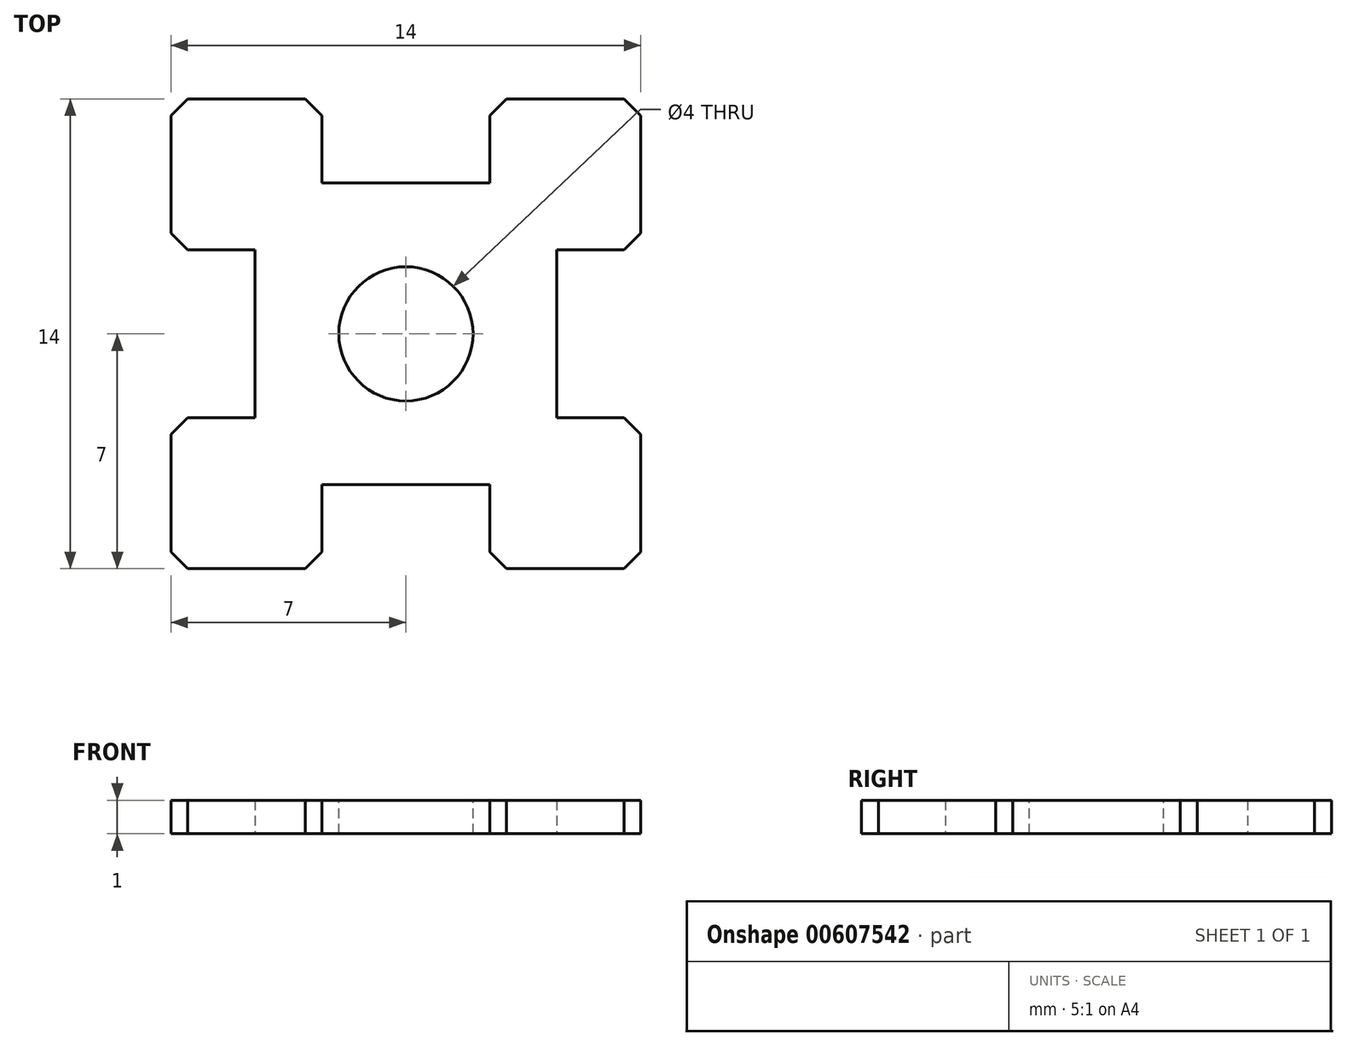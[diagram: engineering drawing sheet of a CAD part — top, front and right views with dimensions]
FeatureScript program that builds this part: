
annotation { "Feature Type Name" : "Feature", "Feature Type Description" : "" }
export const myFeature = defineFeature(function(context is Context, id is Id, definition is map)
    precondition{}
    {
        {
            var Q0;
            Q0=qCreatedBy(makeId("Top.planeOp"),FACE);
            var sketch = newSketch(context, id + "F0", { "sketchPlane" : qUnion([Q0])});
            skLineSegment(sketch, "E0.bottom", {"start": v(-7, -7) * mm, "end": v(-2.5, -7) * mm});
            skLineSegment(sketch, "E0.top", {"start": v(-7, 7) * mm, "end": v(-2.5, 7) * mm});
            skLineSegment(sketch, "E0.left", {"start": v(-7, -7) * mm, "end": v(-7, -2.5) * mm});
            skLineSegment(sketch, "E0.right", {"start": v(7, -7) * mm, "end": v(7, -2.5) * mm});
            skPoint(sketch, "E0.middle", {"position": v(0, 0) * mm});
            skLineSegment(sketch, "E1", {"start": v(0, 7) * mm, "end": v(0, -7) * mm, "construction": true});
            skLineSegment(sketch, "E2", {"start": v(-7, 0) * mm, "end": v(7, 0) * mm, "construction": true});
            skPoint(sketch, "E3.middle", {"position": v(0, -7) * mm});
            skLineSegment(sketch, "E4.top", {"start": v(-4.5, 2.5) * mm, "end": v(-7, 2.5) * mm});
            skLineSegment(sketch, "E4.left", {"start": v(-4.5, -2.5) * mm, "end": v(-4.5, 2.5) * mm});
            skPoint(sketch, "E4.middle", {"position": v(-7, 0) * mm});
            skLineSegment(sketch, "E5.bottom", {"start": v(-2.5, 4.5) * mm, "end": v(2.5, 4.5) * mm});
            skLineSegment(sketch, "E5.left", {"start": v(-2.5, 4.5) * mm, "end": v(-2.5, 7) * mm});
            skLineSegment(sketch, "E5.right", {"start": v(2.5, 4.5) * mm, "end": v(2.5, 7) * mm});
            skPoint(sketch, "E5.middle", {"position": v(0, 7) * mm});
            skPoint(sketch, "E6.middle", {"position": v(7, 0) * mm});
            skPoint(sketch, "E6.right.end.orphan", {"position": v(9.68, 2.5) * mm});
            skPoint(sketch, "E7.orphan", {"position": v(9.68, -2.5) * mm});
            skPoint(sketch, "E8.orphan", {"position": v(4.32, 2.5) * mm});
            skPoint(sketch, "E6.left.start.orphan", {"position": v(4.32, -2.5) * mm});
            skPoint(sketch, "E9.orphan", {"position": v(2.5, -4.92) * mm});
            skPoint(sketch, "E3.top.end.orphan", {"position": v(2.5, -9.08) * mm});
            skPoint(sketch, "E10.orphan", {"position": v(-2.5, -9.08) * mm});
            skPoint(sketch, "E3.left.start.orphan", {"position": v(-2.5, -4.92) * mm});
            skLineSegment(sketch, "E11.MirrorCS", {"start": v(4.5, -2.5) * mm, "end": v(4.5, 2.5) * mm});
            skLineSegment(sketch, "E12.MirrorCS", {"start": v(4.5, 2.5) * mm, "end": v(7, 2.5) * mm});
            skLineSegment(sketch, "E13.MirrorCS", {"start": v(4.5, -2.5) * mm, "end": v(4.5, 2.5) * mm, "construction": true});
            skLineSegment(sketch, "E14.MirrorCS", {"start": v(4.5, -2.5) * mm, "end": v(7, -2.5) * mm});
            skLineSegment(sketch, "E15.MirrorCS", {"start": v(-2.5, -4.5) * mm, "end": v(2.5, -4.5) * mm});
            skLineSegment(sketch, "E16.MirrorCS", {"start": v(-2.5, -4.5) * mm, "end": v(-2.5, -7) * mm});
            skLineSegment(sketch, "E17.MirrorCS", {"start": v(2.5, -4.5) * mm, "end": v(2.5, -7) * mm});
            skPoint(sketch, "E5.top.start.orphan", {"position": v(-2.5, 9.5) * mm});
            skPoint(sketch, "E18.orphan", {"position": v(2.5, 9.5) * mm});
            skPoint(sketch, "E19.orphan", {"position": v(9.5, 2.5) * mm});
            skPoint(sketch, "E20.orphan", {"position": v(9.5, -2.5) * mm});
            skLineSegment(sketch, "E21.trimOffspring", {"start": v(2.5, -9.08) * mm, "end": v(2.5, -9.5) * mm, "construction": true});
            skPoint(sketch, "E22.MirrorCS.end.orphan", {"position": v(2.5, -9.5) * mm});
            skPoint(sketch, "E22.MirrorCS.start.orphan", {"position": v(-2.5, -9.5) * mm});
            skLineSegment(sketch, "E23.trimOffspring", {"start": v(-2.5, -9.08) * mm, "end": v(-2.5, -9.5) * mm, "construction": true});
            skPoint(sketch, "E4.bottom.end.orphan", {"position": v(-9.5, -2.5) * mm});
            skPoint(sketch, "E24.orphan", {"position": v(-9.5, 2.5) * mm});
            skLineSegment(sketch, "E25", {"start": v(-4.5, -2.5) * mm, "end": v(-7, -2.5) * mm});
            skLineSegment(sketch, "E26.trimOffspring", {"start": v(2.5, 7) * mm, "end": v(7, 7) * mm});
            skLineSegment(sketch, "E27.trimOffspring", {"start": v(-7, 2.5) * mm, "end": v(-7, 7) * mm});
            skLineSegment(sketch, "E28.trimOffspring", {"start": v(2.5, -7) * mm, "end": v(7, -7) * mm});
            skLineSegment(sketch, "E29.trimOffspring", {"start": v(7, 2.5) * mm, "end": v(7, 7) * mm});
            skSolve(sketch);
        }
        {
            var Q0;
            Q0=makeQuery(id+"F0.imprint","IMPRINT",FACE,{"disambiguationData":[TD([[makeQuery(id+"F0.imprint","IMPRINT",EDGE,{"derivedFrom":sQuery(id+"F0.wireOp",EDGE,"E0.top")}),-1.0]])]});
            extrude(context, id + "F1", {"entities" : qUnion([Q0]), "depth" : 1 * mm, "offsetDistance" : 25 * mm});
        }
        {
            var Q0;
            Q0=makeQuery(id+"F1.opExtrude","SWEPT_EDGE",EDGE,{"disambiguationData":[OSD([sQuery(id+"F0.wireOp",EDGE,"E0.left"),sQuery(id+"F0.wireOp",EDGE,"E0.bottom")])]});
            var Q1;
            Q1=makeQuery(id+"F1.opExtrude","SWEPT_EDGE",EDGE,{"disambiguationData":[OSD([sQuery(id+"F0.wireOp",EDGE,"E0.bottom"),sQuery(id+"F0.wireOp",EDGE,"E16.MirrorCS")])]});
            var Q2;
            Q2=makeQuery(id+"F1.opExtrude","SWEPT_EDGE",EDGE,{"disambiguationData":[OSD([sQuery(id+"F0.wireOp",EDGE,"E0.left"),sQuery(id+"F0.wireOp",EDGE,"E25")])]});
            var Q3;
            Q3=makeQuery(id+"F1.opExtrude","SWEPT_EDGE",EDGE,{"disambiguationData":[OSD([sQuery(id+"F0.wireOp",EDGE,"E4.top"),sQuery(id+"F0.wireOp",EDGE,"E27.trimOffspring")])]});
            var Q4;
            Q4=makeQuery(id+"F1.opExtrude","SWEPT_EDGE",EDGE,{"disambiguationData":[OSD([sQuery(id+"F0.wireOp",EDGE,"E0.top"),sQuery(id+"F0.wireOp",EDGE,"E27.trimOffspring")])]});
            var Q5;
            Q5=makeQuery(id+"F1.opExtrude","SWEPT_EDGE",EDGE,{"disambiguationData":[OSD([sQuery(id+"F0.wireOp",EDGE,"E0.top"),sQuery(id+"F0.wireOp",EDGE,"E5.left")])]});
            var Q6;
            Q6=makeQuery(id+"F1.opExtrude","SWEPT_EDGE",EDGE,{"disambiguationData":[OSD([sQuery(id+"F0.wireOp",EDGE,"E5.right"),sQuery(id+"F0.wireOp",EDGE,"E26.trimOffspring")])]});
            var Q7;
            Q7=makeQuery(id+"F1.opExtrude","SWEPT_EDGE",EDGE,{"disambiguationData":[OSD([sQuery(id+"F0.wireOp",EDGE,"E26.trimOffspring"),sQuery(id+"F0.wireOp",EDGE,"E29.trimOffspring")])]});
            var Q8;
            Q8=makeQuery(id+"F1.opExtrude","SWEPT_EDGE",EDGE,{"disambiguationData":[OSD([sQuery(id+"F0.wireOp",EDGE,"E0.right"),sQuery(id+"F0.wireOp",EDGE,"E14.MirrorCS")])]});
            var Q9;
            Q9=makeQuery(id+"F1.opExtrude","SWEPT_EDGE",EDGE,{"disambiguationData":[OSD([sQuery(id+"F0.wireOp",EDGE,"E0.right"),sQuery(id+"F0.wireOp",EDGE,"E28.trimOffspring")])]});
            var Q10;
            Q10=makeQuery(id+"F1.opExtrude","SWEPT_EDGE",EDGE,{"disambiguationData":[OSD([sQuery(id+"F0.wireOp",EDGE,"E17.MirrorCS"),sQuery(id+"F0.wireOp",EDGE,"E28.trimOffspring")])]});
            var Q11;
            Q11=makeQuery(id+"F1.opExtrude","SWEPT_EDGE",EDGE,{"disambiguationData":[OSD([sQuery(id+"F0.wireOp",EDGE,"E12.MirrorCS"),sQuery(id+"F0.wireOp",EDGE,"E29.trimOffspring")])]});
            chamfer(context, id + "F2", {"entities" : qUnion([Q0, Q1, Q2, Q3, Q4, Q5, Q6, Q7, Q8, Q9, Q10, Q11]), "width" : 0.5 * mm, "tangentPropagation" : true});
        }
        {
            var Q0;
            Q0=makeQuery(id+"F1.opExtrude","CAP_FACE",FACE,{"disambiguationData":[OSD([sQuery(id+"F0.wireOp",EDGE,"E0.top"),sQuery(id+"F0.wireOp",EDGE,"E0.left"),sQuery(id+"F0.wireOp",EDGE,"E0.right"),sQuery(id+"F0.wireOp",EDGE,"E4.top"),sQuery(id+"F0.wireOp",EDGE,"E4.left"),sQuery(id+"F0.wireOp",EDGE,"E5.bottom"),sQuery(id+"F0.wireOp",EDGE,"E5.left"),sQuery(id+"F0.wireOp",EDGE,"E5.right"),sQuery(id+"F0.wireOp",EDGE,"E11.MirrorCS"),sQuery(id+"F0.wireOp",EDGE,"E12.MirrorCS"),sQuery(id+"F0.wireOp",EDGE,"E14.MirrorCS"),sQuery(id+"F0.wireOp",EDGE,"E15.MirrorCS"),sQuery(id+"F0.wireOp",EDGE,"E0.bottom"),sQuery(id+"F0.wireOp",EDGE,"E16.MirrorCS"),sQuery(id+"F0.wireOp",EDGE,"E17.MirrorCS"),sQuery(id+"F0.wireOp",EDGE,"E25"),sQuery(id+"F0.wireOp",EDGE,"E26.trimOffspring"),sQuery(id+"F0.wireOp",EDGE,"E27.trimOffspring"),sQuery(id+"F0.wireOp",EDGE,"E28.trimOffspring"),sQuery(id+"F0.wireOp",EDGE,"E29.trimOffspring")])],"isStart":false});
            var sketch = newSketch(context, id + "F3", { "sketchPlane" : qUnion([Q0])});
            skCircle(sketch, "E30", {"center": v(0, 0) * mm, "radius": 2 * mm});
            skSolve(sketch);
        }
        {
            var Q0;
            Q0=makeQuery(id+"F3.imprint","IMPRINT",FACE,{"disambiguationData":[TD([[makeQuery(id+"F3.imprint","IMPRINT",EDGE,{"derivedFrom":sQuery(id+"F3.wireOp",EDGE,"E30")}),1.0]])]});
            extrude(context, id + "F4", {"entities" : qUnion([Q0]), "operationType" : NewBodyOperationType.REMOVE, "oppositeDirection" : true, "depth" : 25 * mm, "offsetDistance" : 25 * mm});
        }
    });
